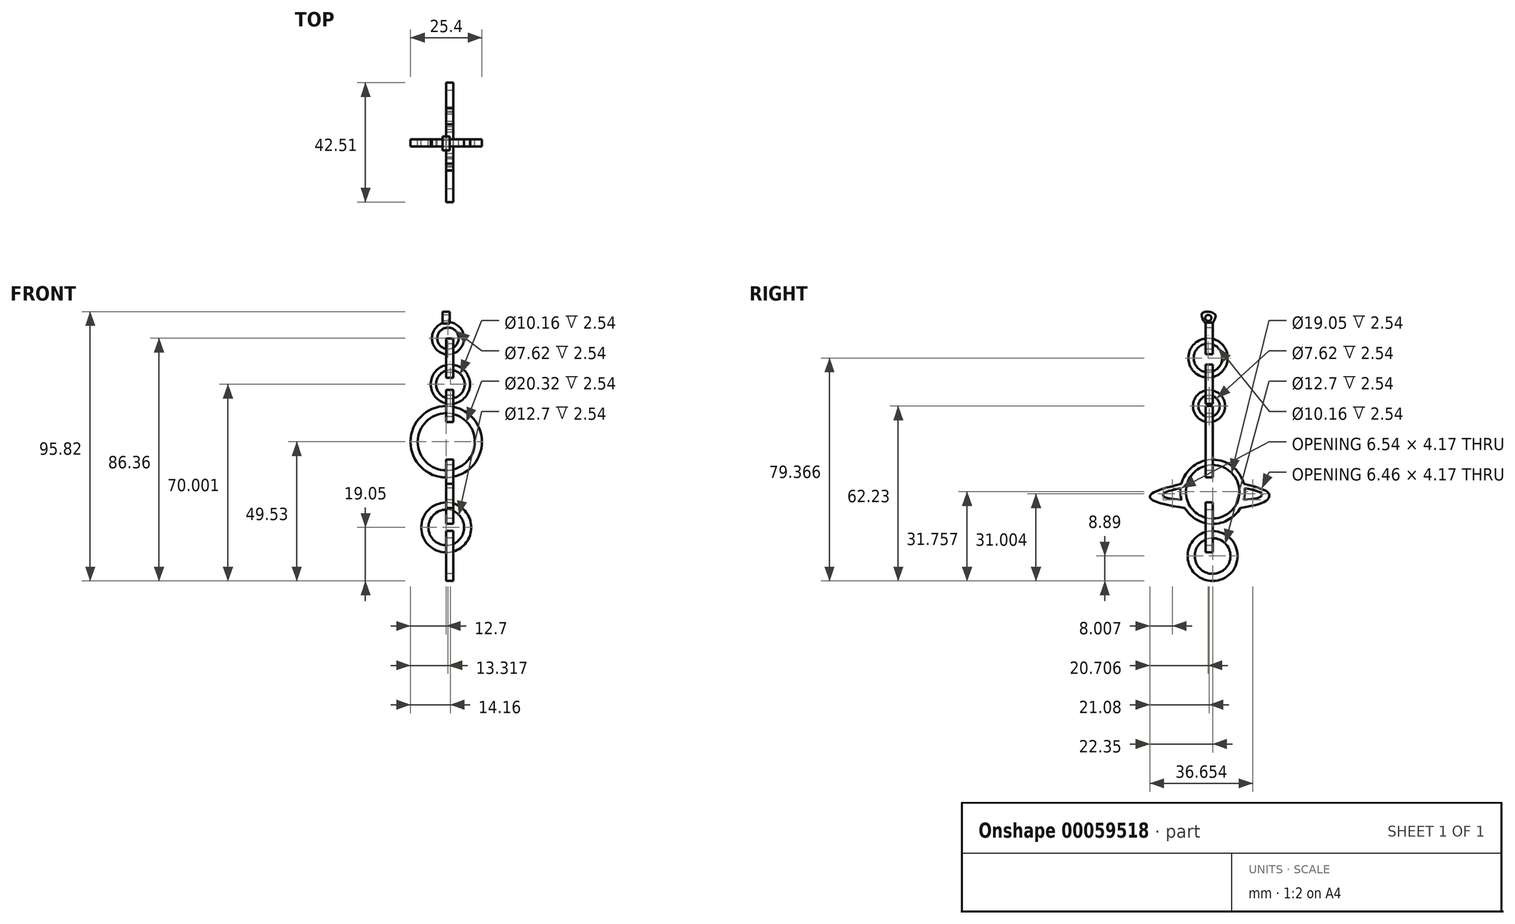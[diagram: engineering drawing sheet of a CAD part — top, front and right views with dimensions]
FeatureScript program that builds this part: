
annotation { "Feature Type Name" : "Feature", "Feature Type Description" : "" }
export const myFeature = defineFeature(function(context is Context, id is Id, definition is map)
    precondition{}
    {
        {
            var Q0;
            Q0=qCreatedBy(makeId("Front.planeOp"),FACE);
            var sketch = newSketch(context, id + "F0", { "sketchPlane" : qUnion([Q0])});
            skCircle(sketch, "E0", {"center": v(0, 0) * mm, "radius": 12.7 * mm});
            skCircle(sketch, "E1", {"center": v(0, 0) * mm, "radius": 10.16 * mm});
            skSolve(sketch);
        }
        {
            var Q0;
            Q0=makeQuery(id+"F0.imprint","IMPRINT",FACE,{"disambiguationData":[TD([[makeQuery(id+"F0.imprint","IMPRINT",EDGE,{"derivedFrom":sQuery(id+"F0.wireOp",EDGE,"E0")}),1.0]])]});
            extrude(context, id + "F1", {"entities" : qUnion([Q0]), "depth" : 2.54 * mm});
        }
        {
            var Q0;
            Q0=qCreatedBy(makeId("Right.planeOp"),FACE);
            var sketch = newSketch(context, id + "F2", { "sketchPlane" : qUnion([Q0])});
            skArc(sketch, "E2", {"start": v(11.07, -20.61) * mm, "mid": v(11.4, -18.54) * mm, "end": v(11.35, -16.44) * mm});
            skCircle(sketch, "E3", {"center": v(0, -17.77) * mm, "radius": 9.53 * mm});
            skFitSpline(sketch, "E4", {"points": [v(9.87, -23.53) * mm, v(20.16, -19.17) * mm, v(11.07, -14.94) * mm], "startDerivative": vector(50.45, 7.44) * mm, "endDerivative": vector(-48.29, 11.4) * mm});
            skFitSpline(sketch, "E5", {"points": [v(11.07, -20.61) * mm, v(17.54, -18.74) * mm, v(11.35, -16.44) * mm], "startDerivative": vector(33.8, 1.68) * mm, "endDerivative": vector(-33.15, 7.44) * mm});
            skArc(sketch, "E6.trimOffspring", {"start": v(11.07, -14.94) * mm, "mid": v(0, -6.34) * mm, "end": v(-11.07, -14.94) * mm});
            skFitSpline(sketch, "E7.MirrorCS", {"points": [v(-11.07, -20.61) * mm, v(-17.61, -18.93) * mm, v(-11.35, -16.44) * mm], "startDerivative": vector(-33.8, 1.68) * mm, "endDerivative": vector(33.15, 7.44) * mm});
            skFitSpline(sketch, "E8.MirrorCS", {"points": [v(-9.87, -23.53) * mm, v(-22.35, -19.53) * mm, v(-11.07, -14.94) * mm], "startDerivative": vector(-50.45, 7.44) * mm, "endDerivative": vector(48.29, 11.4) * mm});
            skArc(sketch, "E9.trimOffspring", {"start": v(-11.35, -16.44) * mm, "mid": v(-11.4, -18.54) * mm, "end": v(-11.07, -20.61) * mm});
            skArc(sketch, "E10.trimOffspring", {"start": v(-9.87, -23.53) * mm, "mid": v(0, -29.2) * mm, "end": v(9.87, -23.53) * mm});
            skSolve(sketch);
        }
        {
            var Q0;
            Q0=makeQuery(id+"F2.imprint","IMPRINT",FACE,{"disambiguationData":[TD([[makeQuery(id+"F2.imprint","IMPRINT",EDGE,{"derivedFrom":sQuery(id+"F2.wireOp",EDGE,"E2")}),1.0]])]});
            extrude(context, id + "F3", {"entities" : qUnion([Q0]), "operationType" : NewBodyOperationType.ADD, "depth" : 2.54 * mm});
        }
        {
            var Q0;
            Q0=qCreatedBy(makeId("Front.planeOp"),FACE);
            var sketch = newSketch(context, id + "F4", { "sketchPlane" : qUnion([Q0])});
            skCircle(sketch, "E11", {"center": v(0, -30.48) * mm, "radius": 6.35 * mm});
            skCircle(sketch, "E12", {"center": v(0, -30.48) * mm, "radius": 8.9 * mm});
            skSolve(sketch);
        }
        {
            var Q0;
            Q0 = qSketchRegion(id + "F4", true);
            extrude(context, id + "F5", {"entities" : qUnion([Q0]), "depth" : 2.54 * mm});
        }
        {
            var Q0;
            Q0=qCreatedBy(makeId("Right.planeOp"),FACE);
            var sketch = newSketch(context, id + "F6", { "sketchPlane" : qUnion([Q0])});
            skCircle(sketch, "E13", {"center": v(0, -40.64) * mm, "radius": 8.9 * mm});
            skCircle(sketch, "E14", {"center": v(0, -40.64) * mm, "radius": 6.35 * mm});
            skSolve(sketch);
        }
        {
            var Q0;
            Q0 = qSketchRegion(id + "F6", true);
            extrude(context, id + "F7", {"entities" : qUnion([Q0]), "depth" : 2.54 * mm});
        }
        {
            var Q0;
            Q0=qCreatedBy(makeId("Right.planeOp"),FACE);
            var sketch = newSketch(context, id + "F8", { "sketchPlane" : qUnion([Q0])});
            skCircle(sketch, "E15", {"center": v(-1.27, 12.7) * mm, "radius": 3.81 * mm});
            skCircle(sketch, "E16", {"center": v(-1.27, 12.7) * mm, "radius": 5.72 * mm});
            skSolve(sketch);
        }
        {
            var Q0;
            Q0 = qSketchRegion(id + "F8", true);
            extrude(context, id + "F9", {"entities" : qUnion([Q0]), "depth" : 2.54 * mm});
        }
        {
            var Q0;
            Q0=qCreatedBy(makeId("Front.planeOp"),FACE);
            var sketch = newSketch(context, id + "F10", { "sketchPlane" : qUnion([Q0])});
            skCircle(sketch, "E17", {"center": v(1.46, 20.47) * mm, "radius": 6.99 * mm});
            skCircle(sketch, "E18", {"center": v(1.46, 20.47) * mm, "radius": 5.08 * mm});
            skSolve(sketch);
        }
        {
            var Q0;
            Q0=makeQuery(id+"F10.imprint","IMPRINT",FACE,{"disambiguationData":[TD([[makeQuery(id+"F10.imprint","IMPRINT",EDGE,{"derivedFrom":sQuery(id+"F10.wireOp",EDGE,"E17")}),1.0]])]});
            extrude(context, id + "F11", {"entities" : qUnion([Q0]), "depth" : 2.54 * mm});
        }
        {
            var Q0;
            Q0=qCreatedBy(makeId("Right.planeOp"),FACE);
            var sketch = newSketch(context, id + "F12", { "sketchPlane" : qUnion([Q0])});
            skCircle(sketch, "E19", {"center": v(-1.64, 29.84) * mm, "radius": 5.08 * mm});
            skCircle(sketch, "E20", {"center": v(-1.64, 29.84) * mm, "radius": 6.99 * mm});
            skSolve(sketch);
        }
        {
            var Q0;
            Q0 = qSketchRegion(id + "F12", true);
            extrude(context, id + "F13", {"entities" : qUnion([Q0]), "operationType" : NewBodyOperationType.ADD, "depth" : 2.54 * mm});
        }
        {
            var Q0;
            Q0=qCreatedBy(makeId("Front.planeOp"),FACE);
            var sketch = newSketch(context, id + "F14", { "sketchPlane" : qUnion([Q0])});
            skCircle(sketch, "E21", {"center": v(0.62, 36.83) * mm, "radius": 3.8 * mm});
            skCircle(sketch, "E22", {"center": v(0.62, 36.83) * mm, "radius": 5.72 * mm});
            skSolve(sketch);
        }
        {
            var Q0;
            Q0 = qSketchRegion(id + "F14", true);
            extrude(context, id + "F15", {"entities" : qUnion([Q0]), "operationType" : NewBodyOperationType.ADD, "depth" : 2.54 * mm});
        }
        {
            var Q0;
            Q0=qCreatedBy(makeId("Right.planeOp"),FACE);
            var sketch = newSketch(context, id + "F16", { "sketchPlane" : qUnion([Q0])});
            skFitSpline(sketch, "E23", {"points": [v(0, 42.24) * mm, v(0.78, 45.44) * mm, v(-3.69, 45.82) * mm, v(-2.19, 41.65) * mm], "startDerivative": vector(7.3, 11.56) * mm, "endDerivative": vector(9.8, -13.33) * mm});
            skLineSegment(sketch, "E24", {"start": v(-2.19, 41.65) * mm, "end": v(0, 42.24) * mm});
            skCircle(sketch, "E25", {"center": v(-1.53, 44.09) * mm, "radius": 1.08 * mm});
            skSolve(sketch);
        }
        {
            var Q0;
            Q0 = qSketchRegion(id + "F16", true);
            extrude(context, id + "F17", {"entities" : qUnion([Q0]), "operationType" : NewBodyOperationType.ADD, "depth" : 1.27 * mm, "hasSecondDirection" : true, "secondDirectionOppositeDirection" : true, "secondDirectionDepth" : 1.27 * mm});
        }
    });
